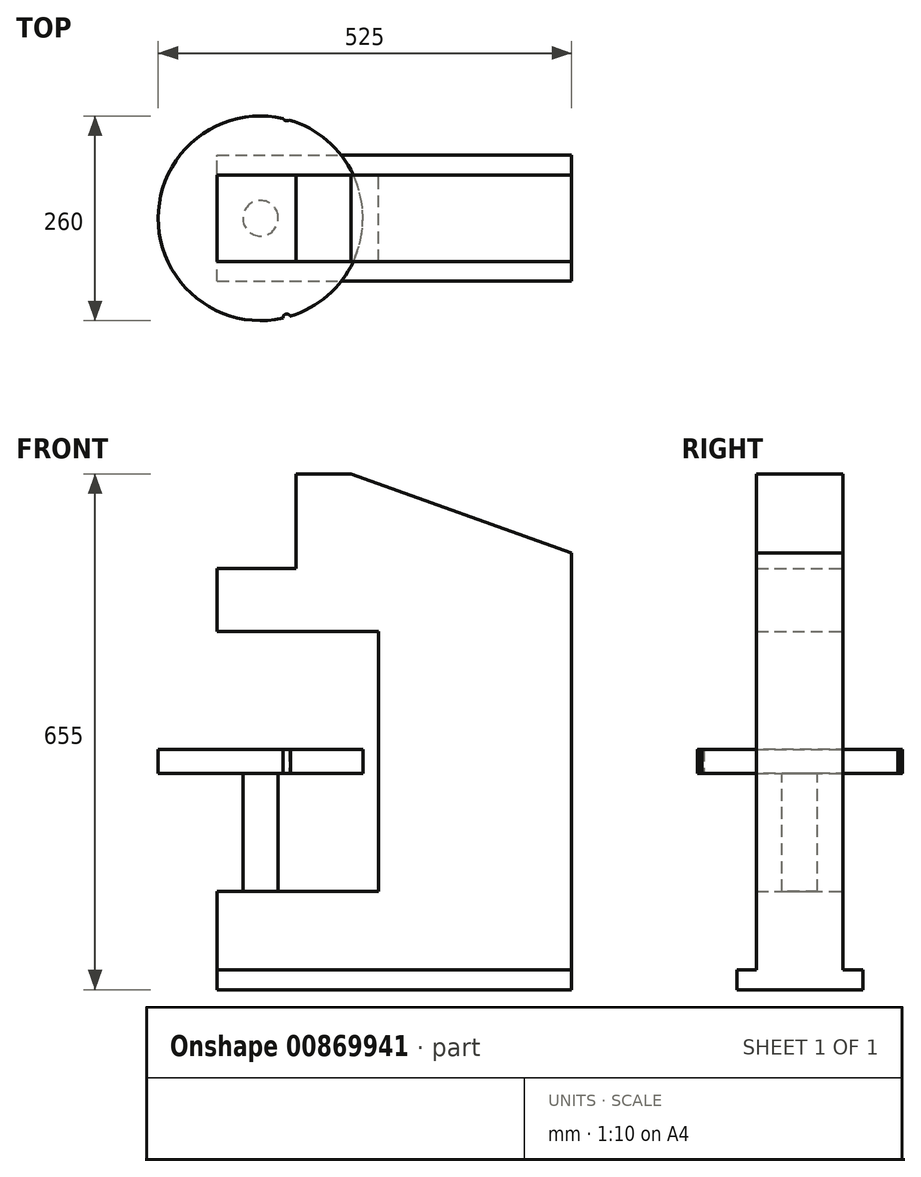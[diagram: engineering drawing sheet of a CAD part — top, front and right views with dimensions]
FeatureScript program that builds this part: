
annotation { "Feature Type Name" : "Feature", "Feature Type Description" : "" }
export const myFeature = defineFeature(function(context is Context, id is Id, definition is map)
    precondition{}
    {
        {
            var Q0;
            Q0=qCreatedBy(makeId("Front.planeOp"),FACE);
            var sketch = newSketch(context, id + "F0", { "sketchPlane" : qUnion([Q0])});
            skLineSegment(sketch, "E0", {"start": v(0, 0) * mm, "end": v(0, 125) * mm});
            skLineSegment(sketch, "E1", {"start": v(0, 125) * mm, "end": v(205, 125) * mm});
            skLineSegment(sketch, "E2", {"start": v(205, 125) * mm, "end": v(205, 455) * mm});
            skLineSegment(sketch, "E3", {"start": v(205, 455) * mm, "end": v(0, 455) * mm});
            skLineSegment(sketch, "E4", {"start": v(0, 455) * mm, "end": v(0, 535) * mm});
            skLineSegment(sketch, "E5", {"start": v(0, 535) * mm, "end": v(100, 535) * mm});
            skLineSegment(sketch, "E6", {"start": v(100, 535) * mm, "end": v(100, 655) * mm});
            skLineSegment(sketch, "E7", {"start": v(100, 655) * mm, "end": v(170, 655) * mm});
            skLineSegment(sketch, "E8", {"start": v(170, 655) * mm, "end": v(450, 555) * mm});
            skLineSegment(sketch, "E9", {"start": v(450, 555) * mm, "end": v(450, 0) * mm});
            skLineSegment(sketch, "E10", {"start": v(450, 0) * mm, "end": v(0, 0) * mm});
            skSolve(sketch);
        }
        {
            var Q0;
            Q0=makeQuery(id+"F0.imprint","IMPRINT",FACE,{"disambiguationData":[TD([[makeQuery(id+"F0.imprint","IMPRINT",EDGE,{"derivedFrom":sQuery(id+"F0.wireOp",EDGE,"E0")}),-1.0]])]});
            extrude(context, id + "F1", {"entities" : qUnion([Q0]), "endBound" : BoundingType.SYMMETRIC, "depth" : 110 * mm, "offsetDistance" : 25 * mm});
        }
        {
            var Q0;
            Q0=qCreatedBy(makeId("Top.planeOp"),FACE);
            var sketch = newSketch(context, id + "F2", { "sketchPlane" : qUnion([Q0])});
            skLineSegment(sketch, "E11.bottom", {"start": v(0, -80) * mm, "end": v(450, -80) * mm});
            skLineSegment(sketch, "E11.top", {"start": v(0, 80) * mm, "end": v(450, 80) * mm});
            skLineSegment(sketch, "E11.left", {"start": v(0, -80) * mm, "end": v(0, 80) * mm});
            skLineSegment(sketch, "E11.right", {"start": v(450, -80) * mm, "end": v(450, 80) * mm});
            skSolve(sketch);
        }
        {
            var Q0;
            Q0=makeQuery(id+"F2.imprint","IMPRINT",FACE,{"disambiguationData":[TD([[makeQuery(id+"F2.imprint","IMPRINT",EDGE,{"derivedFrom":sQuery(id+"F2.wireOp",EDGE,"E11.bottom")}),1.0]])]});
            extrude(context, id + "F3", {"entities" : qUnion([Q0]), "operationType" : NewBodyOperationType.ADD, "depth" : 25 * mm, "offsetDistance" : 25 * mm});
        }
        {
            var Q0;
            Q0=qCreatedBy(makeId("Front.planeOp"),FACE);
            var sketch = newSketch(context, id + "F4", { "sketchPlane" : qUnion([Q0])});
            skLineSegment(sketch, "E12", {"start": v(32.5, 125) * mm, "end": v(32.5, 275) * mm});
            skLineSegment(sketch, "E13", {"start": v(32.5, 275) * mm, "end": v(-75, 275) * mm});
            skLineSegment(sketch, "E14", {"start": v(-75, 275) * mm, "end": v(-75, 305) * mm});
            skLineSegment(sketch, "E15", {"start": v(-75, 305) * mm, "end": v(55, 305) * mm});
            skLineSegment(sketch, "E16", {"start": v(55, 305) * mm, "end": v(55, 125) * mm});
            skLineSegment(sketch, "E17", {"start": v(55, 125) * mm, "end": v(32.5, 125) * mm});
            skSolve(sketch);
        }
        {
            var Q0;
            Q0=makeQuery(id+"F4.imprint","IMPRINT",FACE,{"disambiguationData":[TD([[makeQuery(id+"F4.imprint","IMPRINT",EDGE,{"derivedFrom":sQuery(id+"F4.wireOp",EDGE,"E12")}),-1.0]])]});
            var Q1;
            Q1=sQuery(id+"F4.wireOp",EDGE,"E16");
            revolve(context, id + "F5", {"operationType" : NewBodyOperationType.ADD, "surfaceOperationType" : NewSurfaceOperationType.NEW, "entities" : qUnion([Q0]), "axis" : qUnion([Q1]), "revolveType" : RevolveType.FULL});
        }
        {
            var Q0;
            Q0=qCreatedBy(makeId("Top.planeOp"),FACE);
            var sketch = newSketch(context, id + "F6", { "sketchPlane" : qUnion([Q0])});
            skLineSegment(sketch, "E18.bottom", {"start": v(88.37, -126.62) * mm, "end": v(602.57, -126.62) * mm, "construction": true});
            skLineSegment(sketch, "E18.top", {"start": v(88.37, 128.73) * mm, "end": v(602.57, 128.73) * mm, "construction": true});
            skLineSegment(sketch, "E18.left", {"start": v(88.37, -126.62) * mm, "end": v(88.37, 128.73) * mm, "construction": true});
            skLineSegment(sketch, "E18.right", {"start": v(602.57, -126.62) * mm, "end": v(602.57, 128.73) * mm, "construction": true});
            skSolve(sketch);
        }
        {
            var Q0;
            Q0=sQuery(id+"F6.wireOp",VERTEX,"E18.bottom.start");
            var Q1;
            Q1=sQuery(id+"F6.wireOp",VERTEX,"E18.bottom.end");
            var Q2;
            Q2=sQuery(id+"F6.wireOp",VERTEX,"E18.top.end");
            var Q3;
            Q3=sQuery(id+"F6.wireOp",VERTEX,"E18.top.start");
            var Q4;
            Q4=makeQuery(id+"F1.opExtrude","SWEPT_BODY",BODY,{"disambiguationData":[OSD([sQuery(id+"F0.wireOp",EDGE,"E0"),sQuery(id+"F0.wireOp",EDGE,"E1"),sQuery(id+"F0.wireOp",EDGE,"E2"),sQuery(id+"F0.wireOp",EDGE,"E3"),sQuery(id+"F0.wireOp",EDGE,"E4"),sQuery(id+"F0.wireOp",EDGE,"E5"),sQuery(id+"F0.wireOp",EDGE,"E6"),sQuery(id+"F0.wireOp",EDGE,"E7"),sQuery(id+"F0.wireOp",EDGE,"E8"),sQuery(id+"F0.wireOp",EDGE,"E9"),sQuery(id+"F0.wireOp",EDGE,"E10")])]});
            hole(context, id + "F7", {"style" : HoleStyle.SIMPLE, "endStyle" : HoleEndStyle.THROUGH, "oppositeDirection" : true, "holeDiameter" : 10 * mm, "majorDiameter" : 5 * mm, "isTappedThrough" : true, "tappedDepth" : 12 * mm, "tapClearance" : 3, "locations" : qUnion([Q0, Q1, Q2, Q3]), "scope" : qUnion([Q4])});
        }
    });
